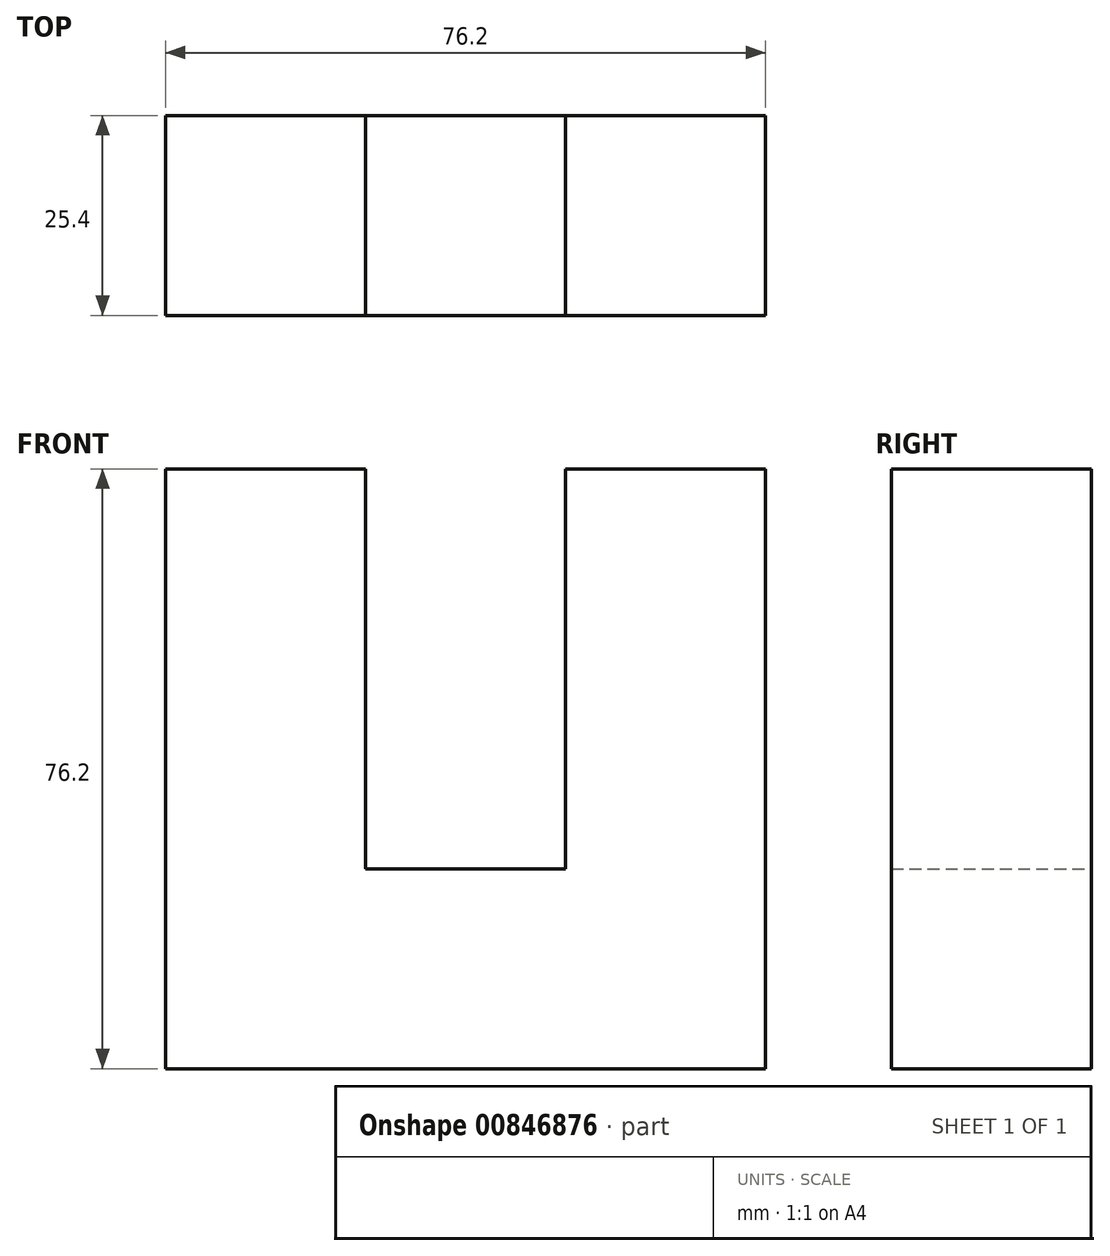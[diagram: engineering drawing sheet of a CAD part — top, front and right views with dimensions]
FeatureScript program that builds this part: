
annotation { "Feature Type Name" : "Feature", "Feature Type Description" : "" }
export const myFeature = defineFeature(function(context is Context, id is Id, definition is map)
    precondition{}
    {
        {
            var Q0;
            Q0=qCreatedBy(makeId("Front.planeOp"),FACE);
            var sketch = newSketch(context, id + "F0", { "sketchPlane" : qUnion([Q0])});
            skLineSegment(sketch, "E0", {"start": v(0, 0) * mm, "end": v(0, 76.2) * mm});
            skLineSegment(sketch, "E1", {"start": v(0, 0) * mm, "end": v(76.2, 0) * mm});
            skLineSegment(sketch, "E2", {"start": v(76.2, 0) * mm, "end": v(76.2, 76.2) * mm});
            skLineSegment(sketch, "E3", {"start": v(0, 76.2) * mm, "end": v(25.4, 76.2) * mm});
            skLineSegment(sketch, "E4", {"start": v(76.2, 76.2) * mm, "end": v(50.8, 76.2) * mm});
            skLineSegment(sketch, "E5", {"start": v(25.4, 76.2) * mm, "end": v(25.4, 25.4) * mm});
            skLineSegment(sketch, "E6", {"start": v(50.8, 76.2) * mm, "end": v(50.8, 25.4) * mm});
            skLineSegment(sketch, "E7", {"start": v(25.4, 25.4) * mm, "end": v(50.8, 25.4) * mm});
            skSolve(sketch);
        }
        {
            var Q0;
            Q0=qSketchRegion(id+"F0",true);
            extrude(context, id + "F1", {"entities" : qUnion([Q0]), "depth" : 25.4 * mm, "offsetDistance" : 25.4 * mm});
        }
    });
